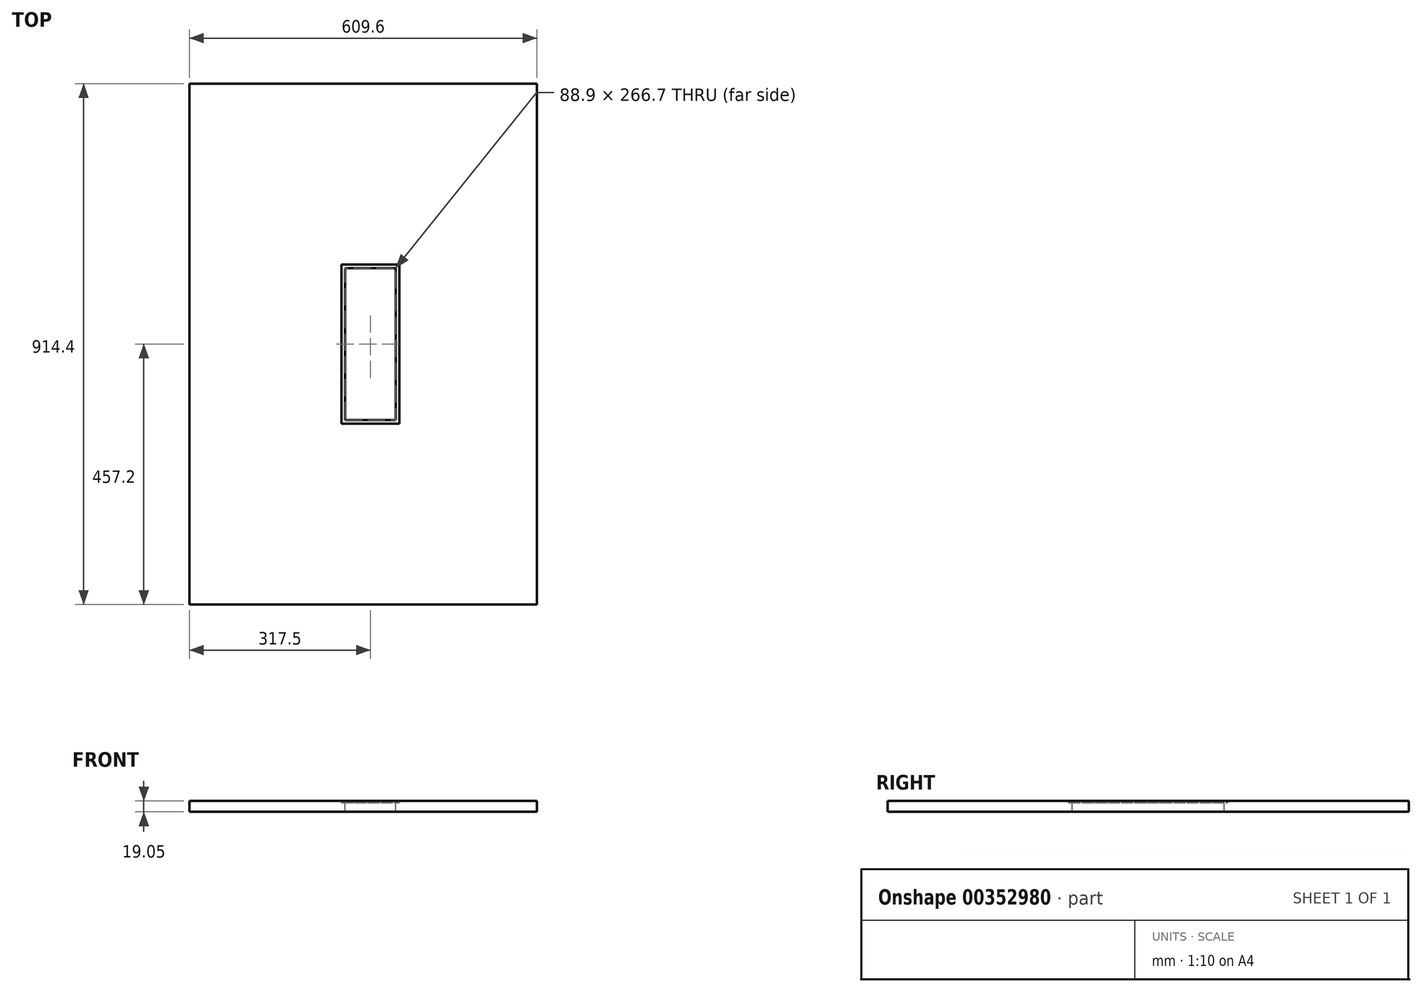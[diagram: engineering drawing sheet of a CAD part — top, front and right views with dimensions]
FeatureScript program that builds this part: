
annotation { "Feature Type Name" : "Feature", "Feature Type Description" : "" }
export const myFeature = defineFeature(function(context is Context, id is Id, definition is map)
    precondition{}
    {
        {
            var Q0;
            Q0=qCreatedBy(makeId("Top.planeOp"),FACE);
            var sketch = newSketch(context, id + "F0", { "sketchPlane" : qUnion([Q0])});
            skLineSegment(sketch, "E0.bottom", {"start": v(-304.8, -457.2) * mm, "end": v(304.8, -457.2) * mm});
            skLineSegment(sketch, "E0.top", {"start": v(-304.8, 457.2) * mm, "end": v(304.8, 457.2) * mm});
            skLineSegment(sketch, "E0.left", {"start": v(-304.8, -457.2) * mm, "end": v(-304.8, 457.2) * mm});
            skLineSegment(sketch, "E0.right", {"start": v(304.8, -457.2) * mm, "end": v(304.8, 457.2) * mm});
            skPoint(sketch, "E0.middle", {"position": v(0, 0) * mm});
            skSolve(sketch);
        }
        {
            var Q0;
            Q0 = qSketchRegion(id + "F0", true);
            extrude(context, id + "F1", {"entities" : qUnion([Q0]), "depth" : 19.05 * mm});
        }
        {
            var Q0;
            Q0=makeQuery(id+"F1.opExtrude","CAP_FACE",FACE,{"disambiguationData":[OSD([sQuery(id+"F0.wireOp",EDGE,"E0.bottom"),sQuery(id+"F0.wireOp",EDGE,"E0.top"),sQuery(id+"F0.wireOp",EDGE,"E0.left"),sQuery(id+"F0.wireOp",EDGE,"E0.right")])],"isStart":false});
            var sketch = newSketch(context, id + "F2", { "sketchPlane" : qUnion([Q0])});
            skLineSegment(sketch, "E1.bottom", {"start": v(-38.1, -139.7) * mm, "end": v(63.5, -139.7) * mm});
            skLineSegment(sketch, "E1.top", {"start": v(-38.1, 139.7) * mm, "end": v(63.5, 139.7) * mm});
            skLineSegment(sketch, "E1.left", {"start": v(-38.1, -139.7) * mm, "end": v(-38.1, 139.7) * mm});
            skLineSegment(sketch, "E1.right", {"start": v(63.5, -139.7) * mm, "end": v(63.5, 139.7) * mm});
            skSolve(sketch);
        }
        {
            var Q0;
            Q0 = qSketchRegion(id + "F2", true);
            extrude(context, id + "F3", {"entities" : qUnion([Q0]), "operationType" : NewBodyOperationType.REMOVE, "oppositeDirection" : true, "depth" : 3.17 * mm});
        }
        {
            var Q0;
            Q0=makeQuery(id+"F3.boolean.opBoolean","COPY",FACE,{"derivedFrom":makeQuery(id+"F3.opExtrude","CAP_FACE",FACE,{"disambiguationData":[OSD([sQuery(id+"F2.wireOp",EDGE,"E1.bottom"),sQuery(id+"F2.wireOp",EDGE,"E1.top"),sQuery(id+"F2.wireOp",EDGE,"E1.left"),sQuery(id+"F2.wireOp",EDGE,"E1.right")])],"isStart":false})});
            var sketch = newSketch(context, id + "F4", { "sketchPlane" : qUnion([Q0])});
            skLineSegment(sketch, "E2.bottom", {"start": v(-31.75, -133.35) * mm, "end": v(57.15, -133.35) * mm});
            skLineSegment(sketch, "E2.top", {"start": v(-31.75, 133.35) * mm, "end": v(57.15, 133.35) * mm});
            skLineSegment(sketch, "E2.left", {"start": v(-31.75, -133.35) * mm, "end": v(-31.75, 133.35) * mm});
            skLineSegment(sketch, "E2.right", {"start": v(57.15, -133.35) * mm, "end": v(57.15, 133.35) * mm});
            skSolve(sketch);
        }
        {
            var Q0;
            Q0 = qSketchRegion(id + "F4", true);
            extrude(context, id + "F5", {"entities" : qUnion([Q0]), "operationType" : NewBodyOperationType.REMOVE, "oppositeDirection" : true, "depth" : 25.4 * mm});
        }
    });
